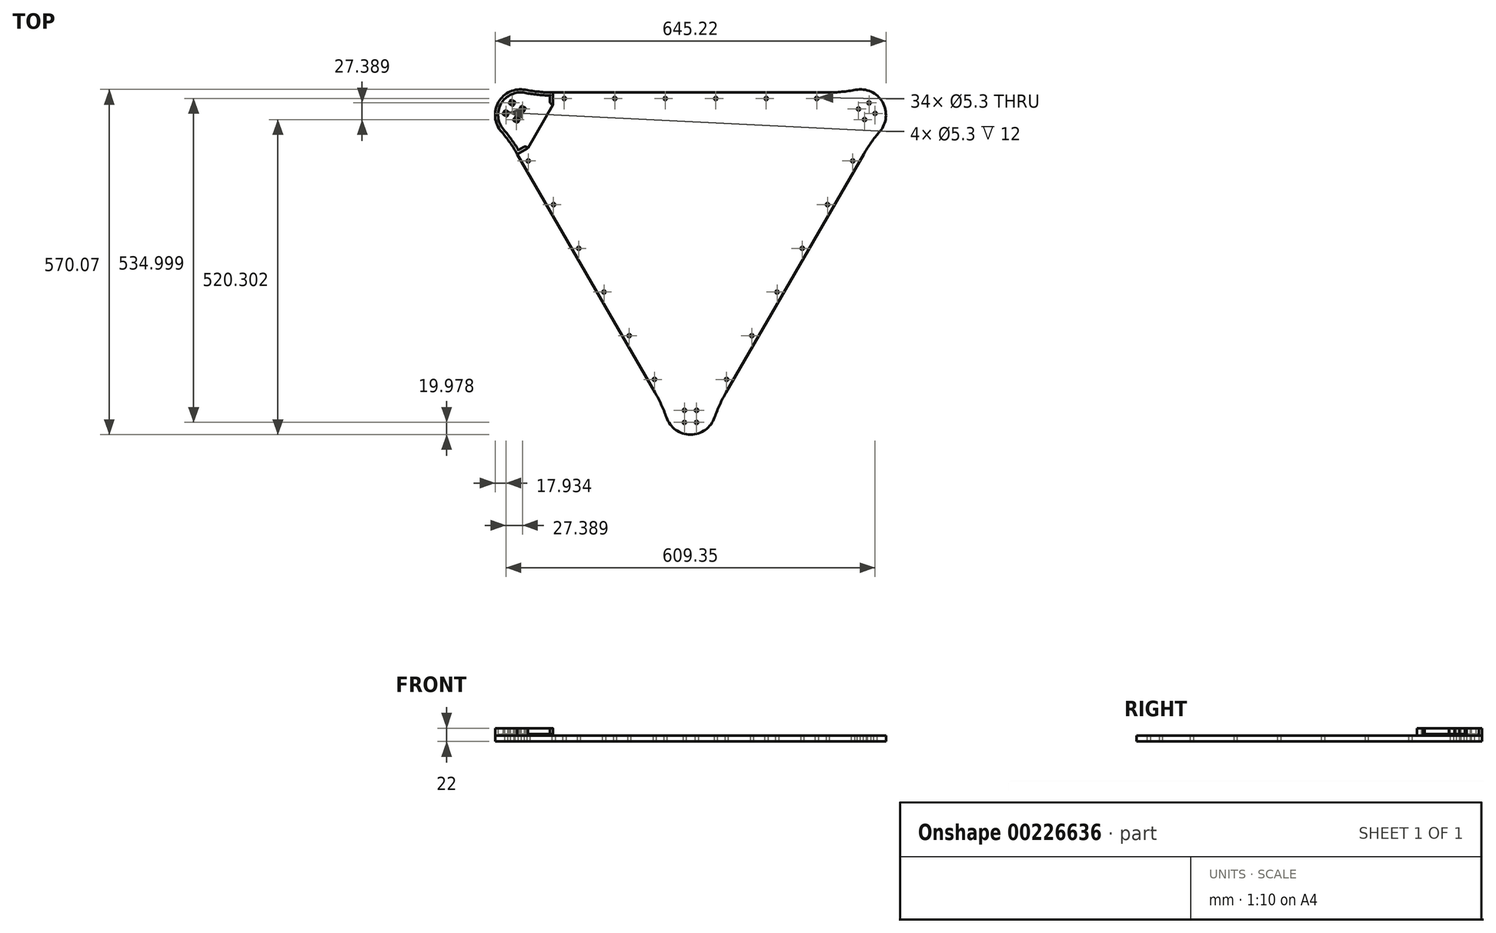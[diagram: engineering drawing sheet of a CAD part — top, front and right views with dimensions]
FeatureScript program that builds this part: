
annotation { "Feature Type Name" : "Feature", "Feature Type Description" : "" }
export const myFeature = defineFeature(function(context is Context, id is Id, definition is map)
    precondition{}
    {
        {
            var Q0;
            Q0=qCreatedBy(makeId("Top.planeOp"),FACE);
            var sketch = newSketch(context, id + "F0", { "sketchPlane" : qUnion([Q0])});
            skLineSegment(sketch, "E0", {"start": v(21.46, 15.98) * mm, "end": v(-18.54, 15.98) * mm});
            skLineSegment(sketch, "E1", {"start": v(-18.54, 15.98) * mm, "end": v(-48.54, 67.94) * mm});
            skLineSegment(sketch, "E2", {"start": v(-18.54, 15.98) * mm, "end": v(-28.54, 15.98) * mm});
            skLineSegment(sketch, "E3", {"start": v(-28.54, 15.98) * mm, "end": v(-58.54, 67.94) * mm});
            skLineSegment(sketch, "E4", {"start": v(-58.54, 67.94) * mm, "end": v(-48.54, 67.94) * mm});
            skLineSegment(sketch, "E5", {"start": v(21.46, 15.98) * mm, "end": v(51.46, 67.94) * mm});
            skLineSegment(sketch, "E6", {"start": v(21.46, 15.98) * mm, "end": v(31.46, 15.98) * mm});
            skLineSegment(sketch, "E7", {"start": v(31.46, 15.98) * mm, "end": v(61.46, 67.94) * mm});
            skLineSegment(sketch, "E8", {"start": v(61.46, 67.94) * mm, "end": v(51.46, 67.94) * mm});
            skLineSegment(sketch, "E9", {"start": v(-28.54, 15.98) * mm, "end": v(-45.86, 5.98) * mm});
            skLineSegment(sketch, "E10", {"start": v(31.46, 15.98) * mm, "end": v(48.78, 5.98) * mm});
            skLineSegment(sketch, "E11", {"start": v(-28.54, 15.98) * mm, "end": v(-28.54, -44.02) * mm});
            skLineSegment(sketch, "E12", {"start": v(-28.54, -44.02) * mm, "end": v(-18.54, -44.02) * mm});
            skLineSegment(sketch, "E13", {"start": v(-18.54, -44.02) * mm, "end": v(21.46, -44.02) * mm});
            skLineSegment(sketch, "E14", {"start": v(31.46, 15.98) * mm, "end": v(31.46, -44.02) * mm});
            skLineSegment(sketch, "E15", {"start": v(31.46, -44.02) * mm, "end": v(21.46, -44.02) * mm});
            skLineSegment(sketch, "E16", {"start": v(-45.86, 5.98) * mm, "end": v(-28.54, -44.02) * mm});
            skLineSegment(sketch, "E17", {"start": v(48.78, 5.98) * mm, "end": v(31.46, -44.02) * mm});
            skLineSegment(sketch, "E18", {"start": v(61.46, 67.94) * mm, "end": v(56.46, 67.94) * mm});
            skLineSegment(sketch, "E19", {"start": v(-58.54, 67.94) * mm, "end": v(-53.54, 67.94) * mm});
            skCircle(sketch, "E20", {"center": v(-53.54, 67.94) * mm, "radius": 12.5 * mm});
            skCircle(sketch, "E21", {"center": v(56.46, 67.94) * mm, "radius": 12.5 * mm});
            skLineSegment(sketch, "E22", {"start": v(35.32, 39.98) * mm, "end": v(-32.4, 39.98) * mm});
            skLineSegment(sketch, "E23", {"start": v(-35.86, 45.98) * mm, "end": v(38.78, 45.98) * mm});
            skLineSegment(sketch, "E24", {"start": v(-28.54, 15.98) * mm, "end": v(-18.6, 15.98) * mm});
            skLineSegment(sketch, "E25", {"start": v(21.5, -34.07) * mm, "end": v(21.5, 6.03) * mm});
            skLineSegment(sketch, "E26", {"start": v(21.5, 6.03) * mm, "end": v(15.97, 6.03) * mm});
            skLineSegment(sketch, "E27", {"start": v(15.97, 6.03) * mm, "end": v(14.18, 6.03) * mm});
            skLineSegment(sketch, "E28", {"start": v(14.18, 6.03) * mm, "end": v(8.78, 6.03) * mm});
            skLineSegment(sketch, "E29", {"start": v(8.78, 6.03) * mm, "end": v(7, 6.03) * mm});
            skLineSegment(sketch, "E30", {"start": v(7, 6.03) * mm, "end": v(-4.08, 6.03) * mm});
            skLineSegment(sketch, "E31", {"start": v(-4.08, 6.03) * mm, "end": v(-5.87, 6.03) * mm});
            skLineSegment(sketch, "E32", {"start": v(-5.87, 6.03) * mm, "end": v(-11.27, 6.03) * mm});
            skLineSegment(sketch, "E33", {"start": v(-11.27, 6.03) * mm, "end": v(-13.06, 6.03) * mm});
            skLineSegment(sketch, "E34", {"start": v(21.5, 6.03) * mm, "end": v(21.5, 4.24) * mm});
            skLineSegment(sketch, "E35", {"start": v(8.78, 4.24) * mm, "end": v(14.18, 4.24) * mm});
            skLineSegment(sketch, "E36", {"start": v(14.18, 4.24) * mm, "end": v(15.97, 6.03) * mm});
            skLineSegment(sketch, "E37", {"start": v(7, 6.03) * mm, "end": v(8.78, 4.24) * mm});
            skLineSegment(sketch, "E38", {"start": v(-5.87, 4.24) * mm, "end": v(-11.27, 4.24) * mm});
            skLineSegment(sketch, "E39", {"start": v(-11.27, 4.24) * mm, "end": v(-13.06, 6.03) * mm});
            skLineSegment(sketch, "E40", {"start": v(-5.87, 4.24) * mm, "end": v(-4.08, 6.03) * mm});
            skLineSegment(sketch, "E41", {"start": v(21.5, -34.07) * mm, "end": v(21.5, -32.28) * mm});
            skLineSegment(sketch, "E42", {"start": v(21.5, -34.07) * mm, "end": v(19.72, -34.07) * mm});
            skLineSegment(sketch, "E43", {"start": v(-18.6, -34.07) * mm, "end": v(-16.8, -34.07) * mm});
            skLineSegment(sketch, "E44", {"start": v(-11.27, -32.28) * mm, "end": v(-5.87, -32.28) * mm});
            skLineSegment(sketch, "E45", {"start": v(-5.87, -32.28) * mm, "end": v(-4.08, -34.07) * mm});
            skLineSegment(sketch, "E46", {"start": v(-11.27, -32.28) * mm, "end": v(-13.06, -34.07) * mm});
            skLineSegment(sketch, "E47", {"start": v(7, -34.07) * mm, "end": v(8.78, -32.28) * mm});
            skLineSegment(sketch, "E48", {"start": v(8.78, -32.28) * mm, "end": v(14.18, -32.28) * mm});
            skLineSegment(sketch, "E49", {"start": v(14.18, -32.28) * mm, "end": v(15.97, -34.07) * mm});
            skLineSegment(sketch, "E50", {"start": v(-18.6, 6.03) * mm, "end": v(-18.6, 0.5) * mm});
            skLineSegment(sketch, "E51", {"start": v(-18.6, 0.5) * mm, "end": v(-18.6, -1.3) * mm});
            skLineSegment(sketch, "E52", {"start": v(-18.6, -1.3) * mm, "end": v(-18.6, -6.7) * mm});
            skLineSegment(sketch, "E53", {"start": v(-18.6, -6.7) * mm, "end": v(-18.6, -8.48) * mm});
            skLineSegment(sketch, "E54", {"start": v(-18.6, -8.48) * mm, "end": v(-18.6, -19.55) * mm});
            skLineSegment(sketch, "E55", {"start": v(-18.6, -19.55) * mm, "end": v(-18.6, -21.34) * mm});
            skLineSegment(sketch, "E56", {"start": v(-18.6, -21.34) * mm, "end": v(-18.6, -26.74) * mm});
            skLineSegment(sketch, "E57", {"start": v(-18.6, -26.74) * mm, "end": v(-18.6, -28.53) * mm});
            skLineSegment(sketch, "E58", {"start": v(-18.6, 0.5) * mm, "end": v(-16.8, -1.3) * mm});
            skLineSegment(sketch, "E59", {"start": v(-16.8, -1.3) * mm, "end": v(-16.8, -6.7) * mm});
            skLineSegment(sketch, "E60", {"start": v(-16.8, -6.7) * mm, "end": v(-18.6, -8.48) * mm});
            skLineSegment(sketch, "E61", {"start": v(-18.6, -19.55) * mm, "end": v(-16.8, -21.34) * mm});
            skLineSegment(sketch, "E62", {"start": v(-16.8, -21.34) * mm, "end": v(-16.8, -26.74) * mm});
            skLineSegment(sketch, "E63", {"start": v(-16.8, -26.74) * mm, "end": v(-18.6, -28.53) * mm});
            skLineSegment(sketch, "E64", {"start": v(21.5, 0.5) * mm, "end": v(19.72, -1.3) * mm});
            skLineSegment(sketch, "E65", {"start": v(19.72, -1.3) * mm, "end": v(19.72, -6.7) * mm});
            skLineSegment(sketch, "E66", {"start": v(19.72, -6.7) * mm, "end": v(21.5, -8.48) * mm});
            skLineSegment(sketch, "E67", {"start": v(21.5, -19.55) * mm, "end": v(19.72, -21.34) * mm});
            skLineSegment(sketch, "E68", {"start": v(19.72, -21.34) * mm, "end": v(19.72, -26.74) * mm});
            skLineSegment(sketch, "E69", {"start": v(19.72, -26.74) * mm, "end": v(21.5, -28.53) * mm});
            skLineSegment(sketch, "E70", {"start": v(-18.6, 6.03) * mm, "end": v(21.5, 6.03) * mm});
            skLineSegment(sketch, "E71", {"start": v(21.5, 6.03) * mm, "end": v(21.5, -34.07) * mm});
            skLineSegment(sketch, "E72", {"start": v(21.5, -34.07) * mm, "end": v(-18.6, -34.07) * mm});
            skLineSegment(sketch, "E73", {"start": v(-18.6, 6.03) * mm, "end": v(-18.6, -34.07) * mm});
            skSolve(sketch);
        }
        {
            var Q0;
            Q0=qCreatedBy(makeId("Top.planeOp"),FACE);
            var sketch = newSketch(context, id + "F1", { "sketchPlane" : qUnion([Q0])});
            skLineSegment(sketch, "E74", {"start": v(-45.86, 5.98) * mm, "end": v(-170.86, 222.49) * mm});
            skLineSegment(sketch, "E75", {"start": v(-170.86, 222.49) * mm, "end": v(-153.54, 232.49) * mm});
            skLineSegment(sketch, "E76", {"start": v(-153.54, 232.49) * mm, "end": v(-28.54, 15.98) * mm});
            skLineSegment(sketch, "E77", {"start": v(-28.54, 15.98) * mm, "end": v(-45.86, 5.98) * mm});
            skLineSegment(sketch, "E78", {"start": v(48.78, 5.98) * mm, "end": v(173.78, 222.49) * mm});
            skLineSegment(sketch, "E79", {"start": v(173.78, 222.49) * mm, "end": v(156.46, 232.49) * mm});
            skLineSegment(sketch, "E80", {"start": v(156.46, 232.49) * mm, "end": v(31.46, 15.98) * mm});
            skLineSegment(sketch, "E81", {"start": v(31.46, 15.98) * mm, "end": v(48.78, 5.98) * mm});
            skLineSegment(sketch, "E82", {"start": v(-153.54, 232.49) * mm, "end": v(1.46, 321.98) * mm});
            skLineSegment(sketch, "E83", {"start": v(1.46, 321.98) * mm, "end": v(156.46, 232.49) * mm});
            skLineSegment(sketch, "E84", {"start": v(-45.86, 5.98) * mm, "end": v(-28.54, -44.02) * mm});
            skLineSegment(sketch, "E85", {"start": v(-28.54, -44.02) * mm, "end": v(31.46, -44.02) * mm});
            skLineSegment(sketch, "E86", {"start": v(31.46, -44.02) * mm, "end": v(48.78, 5.98) * mm});
            skCircle(sketch, "E87", {"center": v(60.95, 47.07) * mm, "radius": 2.65 * mm});
            skCircle(sketch, "E88", {"center": v(102.62, 119.24) * mm, "radius": 2.65 * mm});
            skLineSegment(sketch, "E89", {"start": v(60.95, 47.07) * mm, "end": v(102.62, 119.24) * mm});
            skPoint(sketch, "E90", {"position": v(81.79, 83.15) * mm});
            skCircle(sketch, "E91", {"center": v(144.29, 191.4) * mm, "radius": 2.65 * mm});
            skLineSegment(sketch, "E92", {"start": v(144.29, 191.4) * mm, "end": v(102.62, 119.24) * mm});
            skCircle(sketch, "E93", {"center": v(-141.37, 191.4) * mm, "radius": 2.65 * mm});
            skCircle(sketch, "E94", {"center": v(-99.7, 119.24) * mm, "radius": 2.65 * mm});
            skCircle(sketch, "E95", {"center": v(-58.03, 47.07) * mm, "radius": 2.65 * mm});
            skLineSegment(sketch, "E96", {"start": v(-141.37, 191.4) * mm, "end": v(-99.7, 119.24) * mm});
            skLineSegment(sketch, "E97", {"start": v(-99.7, 119.24) * mm, "end": v(-58.03, 47.07) * mm});
            skCircle(sketch, "E98", {"center": v(-8.57, -4) * mm, "radius": 2.65 * mm});
            skCircle(sketch, "E99", {"center": v(11.48, -4) * mm, "radius": 2.65 * mm});
            skCircle(sketch, "E100", {"center": v(-8.57, -24.04) * mm, "radius": 2.65 * mm});
            skCircle(sketch, "E101", {"center": v(11.48, -24.04) * mm, "radius": 2.65 * mm});
            skPoint(sketch, "E102", {"position": v(-8.57, 4.24) * mm});
            skPoint(sketch, "E103", {"position": v(11.48, 4.24) * mm});
            skPoint(sketch, "E104", {"position": v(-16.8, -4) * mm});
            skPoint(sketch, "E105", {"position": v(-16.8, -24.04) * mm});
            skArc(sketch, "E106", {"start": v(-38.36, -15.67) * mm, "mid": v(1.46, -44.02) * mm, "end": v(41.28, -15.67) * mm});
            skSolve(sketch);
        }
        {
            var Q0;
            Q0=makeQuery(id+"F1.imprint","IMPRINT",FACE,{"disambiguationData":[TD([[makeQuery(id+"F1.imprint","IMPRINT",EDGE,{"derivedFrom":sQuery(id+"F1.wireOp",EDGE,"E76")}),1.0]])]});
            var Q1;
            Q1=makeQuery(id+"F1.imprint","IMPRINT",FACE,{"disambiguationData":[TD([[makeQuery(id+"F1.imprint","IMPRINT",EDGE,{"derivedFrom":sQuery(id+"F1.wireOp",EDGE,"E74")}),-1.0]])]});
            var Q2;
            Q2=makeQuery(id+"F1.imprint","IMPRINT",FACE,{"disambiguationData":[TD([[makeQuery(id+"F1.imprint","IMPRINT",EDGE,{"derivedFrom":sQuery(id+"F1.wireOp",EDGE,"E78")}),1.0]])]});
            extrude(context, id + "F2", {"entities" : qUnion([Q0, Q1, Q2]), "depth" : 10 * mm});
        }
        {
            var Q0;
            Q0=makeQuery(id+"F2.opExtrude","SWEPT_EDGE",EDGE,{"disambiguationData":[OSD([sQuery(id+"F1.wireOp",EDGE,"E78"),sQuery(id+"F1.wireOp",EDGE,"E81"),sQuery(id+"F1.wireOp",EDGE,"E86")])]});
            var Q1;
            Q1=makeQuery(id+"F2.opExtrude","SWEPT_EDGE",EDGE,{"disambiguationData":[OSD([sQuery(id+"F1.wireOp",EDGE,"E74"),sQuery(id+"F1.wireOp",EDGE,"E77"),sQuery(id+"F1.wireOp",EDGE,"E84")])]});
            fillet(context, id + "F3", {"entities" : qUnion([Q0, Q1]), "radius" : 240 * mm, "tangentPropagation" : true, "allowEdgeOverflow" : false});
        }
        {
            var Q0;
            Q0=makeQuery(id+"F2.opExtrude","SWEPT_BODY",BODY,{"disambiguationData":[OSD([sQuery(id+"F1.wireOp",EDGE,"E74"),sQuery(id+"F1.wireOp",EDGE,"E75"),sQuery(id+"F1.wireOp",EDGE,"E78"),sQuery(id+"F1.wireOp",EDGE,"E79"),sQuery(id+"F1.wireOp",EDGE,"E82"),sQuery(id+"F1.wireOp",EDGE,"E83"),sQuery(id+"F1.wireOp",EDGE,"E84"),sQuery(id+"F1.wireOp",EDGE,"E85"),sQuery(id+"F1.wireOp",EDGE,"E86"),sQuery(id+"F1.wireOp",EDGE,"E87"),sQuery(id+"F1.wireOp",EDGE,"E88"),sQuery(id+"F1.wireOp",EDGE,"E91"),sQuery(id+"F1.wireOp",EDGE,"E93"),sQuery(id+"F1.wireOp",EDGE,"E94"),sQuery(id+"F1.wireOp",EDGE,"E95"),sQuery(id+"F1.wireOp",EDGE,"E98"),sQuery(id+"F1.wireOp",EDGE,"E99"),sQuery(id+"F1.wireOp",EDGE,"E100"),sQuery(id+"F1.wireOp",EDGE,"E101")])]});
            var Q1;
            Q1=makeQuery(id+"F2.opExtrude","SWEPT_EDGE",EDGE,{"disambiguationData":[OSD([sQuery(id+"F1.wireOp",EDGE,"E82"),sQuery(id+"F1.wireOp",EDGE,"E83")])]});
            circularPattern(context, id + "F4", {"operationType" : NewBodyOperationType.ADD, "entities" : qUnion([Q0]), "axis" : qUnion([Q1]), "angle" : 360 * degree, "instanceCount" : 3, "equalSpace" : true});
        }
        {
            var Q0;
            {var subQ0=makeQuery(id+"F2.opExtrude","CAP_FACE",FACE,{"disambiguationData":[OSD([sQuery(id+"F1.wireOp",EDGE,"E74"),sQuery(id+"F1.wireOp",EDGE,"E75"),sQuery(id+"F1.wireOp",EDGE,"E78"),sQuery(id+"F1.wireOp",EDGE,"E79"),sQuery(id+"F1.wireOp",EDGE,"E82"),sQuery(id+"F1.wireOp",EDGE,"E83"),sQuery(id+"F1.wireOp",EDGE,"E84"),sQuery(id+"F1.wireOp",EDGE,"E86"),sQuery(id+"F1.wireOp",EDGE,"E87"),sQuery(id+"F1.wireOp",EDGE,"E88"),sQuery(id+"F1.wireOp",EDGE,"E91"),sQuery(id+"F1.wireOp",EDGE,"E93"),sQuery(id+"F1.wireOp",EDGE,"E94"),sQuery(id+"F1.wireOp",EDGE,"E95"),sQuery(id+"F1.wireOp",EDGE,"E98"),sQuery(id+"F1.wireOp",EDGE,"E99"),sQuery(id+"F1.wireOp",EDGE,"E100"),sQuery(id+"F1.wireOp",EDGE,"E101"),sQuery(id+"F1.wireOp",EDGE,"E106")])],"isStart":false});Q0=makeQuery(id+"F4.boolean.opBoolean","MERGE",FACE,{"derivedFrom":[subQ0,makeQuery(id+"F4.opPattern","COPY",FACE,{"derivedFrom":subQ0,"instanceName":"1"}),makeQuery(id+"F4.opPattern","COPY",FACE,{"derivedFrom":subQ0,"instanceName":"2"})]});}
            var sketch = newSketch(context, id + "F5", { "sketchPlane" : qUnion([Q0])});
            skArc(sketch, "E107", {"start": v(-271.01, 525.28) * mm, "mid": v(-315.5, 504.98) * mm, "end": v(-310.84, 456.3) * mm});
            skArc(sketch, "E108", {"start": v(313.78, 456.32) * mm, "mid": v(318.42, 504.98) * mm, "end": v(273.96, 525.29) * mm});
            skArc(sketch, "E109", {"start": v(-38.36, -15.67) * mm, "mid": v(1.47, -44.02) * mm, "end": v(41.29, -15.64) * mm});
            skArc(sketch, "E110", {"start": v(-38.36, -15.67) * mm, "mid": v(-46.84, 5.52) * mm, "end": v(-57.3, 25.8) * mm});
            skArc(sketch, "E111", {"start": v(60.22, 25.8) * mm, "mid": v(49.77, 5.53) * mm, "end": v(41.29, -15.64) * mm});
            skArc(sketch, "E112", {"start": v(-284.42, 419.18) * mm, "mid": v(-296.75, 438.36) * mm, "end": v(-310.84, 456.3) * mm});
            skArc(sketch, "E113", {"start": v(-271.01, 525.28) * mm, "mid": v(-248.44, 522.04) * mm, "end": v(-225.66, 520.96) * mm});
            skArc(sketch, "E114", {"start": v(228.58, 520.96) * mm, "mid": v(251.37, 522.04) * mm, "end": v(273.96, 525.29) * mm});
            skArc(sketch, "E115", {"start": v(313.78, 456.32) * mm, "mid": v(299.68, 438.38) * mm, "end": v(287.34, 419.18) * mm});
            skLineSegment(sketch, "E116", {"start": v(60.22, 25.8) * mm, "end": v(287.34, 419.18) * mm});
            skLineSegment(sketch, "E117", {"start": v(228.58, 520.96) * mm, "end": v(-225.66, 520.96) * mm});
            skLineSegment(sketch, "E118", {"start": v(-284.42, 419.18) * mm, "end": v(-57.3, 25.8) * mm});
            skCircle(sketch, "E119", {"center": v(-8.57, -24.04) * mm, "radius": 2.65 * mm});
            skCircle(sketch, "E120", {"center": v(11.48, -24.04) * mm, "radius": 2.65 * mm});
            skCircle(sketch, "E121", {"center": v(-8.57, -4) * mm, "radius": 2.65 * mm});
            skCircle(sketch, "E122", {"center": v(60.95, 47.07) * mm, "radius": 2.65 * mm});
            skCircle(sketch, "E123", {"center": v(102.62, 119.24) * mm, "radius": 2.65 * mm});
            skCircle(sketch, "E124", {"center": v(144.29, 191.4) * mm, "radius": 2.65 * mm});
            skCircle(sketch, "E125", {"center": v(185.95, 263.57) * mm, "radius": 2.65 * mm});
            skCircle(sketch, "E126", {"center": v(227.62, 335.74) * mm, "radius": 2.65 * mm});
            skCircle(sketch, "E127", {"center": v(269.29, 407.91) * mm, "radius": 2.65 * mm});
            skCircle(sketch, "E128", {"center": v(288.77, 476.28) * mm, "radius": 2.65 * mm});
            skCircle(sketch, "E129", {"center": v(306.13, 486.3) * mm, "radius": 2.65 * mm});
            skCircle(sketch, "E130", {"center": v(296.1, 503.67) * mm, "radius": 2.65 * mm});
            skCircle(sketch, "E131", {"center": v(278.75, 493.65) * mm, "radius": 2.65 * mm});
            skCircle(sketch, "E132", {"center": v(209.8, 510.96) * mm, "radius": 2.65 * mm});
            skCircle(sketch, "E133", {"center": v(126.46, 510.96) * mm, "radius": 2.65 * mm});
            skCircle(sketch, "E134", {"center": v(43.13, 510.96) * mm, "radius": 2.65 * mm});
            skCircle(sketch, "E135", {"center": v(-40.2, 510.96) * mm, "radius": 2.65 * mm});
            skCircle(sketch, "E136", {"center": v(-123.54, 510.96) * mm, "radius": 2.65 * mm});
            skCircle(sketch, "E137", {"center": v(-206.87, 510.96) * mm, "radius": 2.65 * mm});
            skCircle(sketch, "E138", {"center": v(-293.2, 503.67) * mm, "radius": 2.65 * mm});
            skCircle(sketch, "E139", {"center": v(-275.83, 493.65) * mm, "radius": 2.65 * mm});
            skCircle(sketch, "E140", {"center": v(-303.22, 486.3) * mm, "radius": 2.65 * mm});
            skCircle(sketch, "E141", {"center": v(-285.85, 476.28) * mm, "radius": 2.65 * mm});
            skCircle(sketch, "E142", {"center": v(-266.37, 407.91) * mm, "radius": 2.65 * mm});
            skCircle(sketch, "E143", {"center": v(-224.7, 335.74) * mm, "radius": 2.65 * mm});
            skCircle(sketch, "E144", {"center": v(-183.03, 263.57) * mm, "radius": 2.65 * mm});
            skCircle(sketch, "E145", {"center": v(-141.37, 191.4) * mm, "radius": 2.65 * mm});
            skCircle(sketch, "E146", {"center": v(-99.7, 119.24) * mm, "radius": 2.65 * mm});
            skCircle(sketch, "E147", {"center": v(-58.03, 47.07) * mm, "radius": 2.65 * mm});
            skCircle(sketch, "E148", {"center": v(11.48, -4) * mm, "radius": 2.65 * mm});
            skLineSegment(sketch, "E149", {"start": v(-284.42, 419.18) * mm, "end": v(-267.1, 429.18) * mm});
            skPoint(sketch, "E150", {"position": v(-275.76, 424.18) * mm});
            skLineSegment(sketch, "E151", {"start": v(-57.3, 25.8) * mm, "end": v(-39.98, 35.8) * mm});
            skLineSegment(sketch, "E152", {"start": v(-39.98, 35.8) * mm, "end": v(-267.1, 429.18) * mm});
            skPoint(sketch, "E153", {"position": v(-48.64, 30.8) * mm});
            skLineSegment(sketch, "E154", {"start": v(-48.64, 30.8) * mm, "end": v(-275.76, 424.18) * mm});
            skLineSegment(sketch, "E155", {"start": v(60.22, 25.8) * mm, "end": v(42.9, 35.8) * mm});
            skLineSegment(sketch, "E156", {"start": v(42.9, 35.8) * mm, "end": v(270.02, 429.18) * mm});
            skLineSegment(sketch, "E157", {"start": v(270.02, 429.18) * mm, "end": v(287.34, 419.18) * mm});
            skLineSegment(sketch, "E158", {"start": v(278.68, 424.18) * mm, "end": v(51.56, 30.8) * mm});
            skLineSegment(sketch, "E159", {"start": v(-225.66, 520.96) * mm, "end": v(-225.66, 500.96) * mm});
            skLineSegment(sketch, "E160", {"start": v(-225.66, 500.96) * mm, "end": v(228.58, 500.96) * mm});
            skLineSegment(sketch, "E161", {"start": v(228.58, 500.96) * mm, "end": v(228.58, 520.96) * mm});
            skLineSegment(sketch, "E162", {"start": v(-225.66, 510.96) * mm, "end": v(228.58, 510.96) * mm});
            skSolve(sketch);
        }
        {
            var Q0;
            {var subQ12=sQuery(id+"F5.wireOp",EDGE,"E108");Q0=makeQuery(id+"F5.imprint","IMPRINT",FACE,{"disambiguationData":[TD([[makeQuery(id+"F5.imprint","IMPRINT",EDGE,{"derivedFrom":subQ12}),1.0]])]});}
            var sketch = newSketch(context, id + "F6", { "sketchPlane" : qUnion([Q0])});
            skLineSegment(sketch, "E163.bottom", {"start": v(-321.15, 526.05) * mm, "end": v(324.07, 526.05) * mm});
            skLineSegment(sketch, "E163.top", {"start": v(-321.15, -44.02) * mm, "end": v(324.07, -44.02) * mm});
            skLineSegment(sketch, "E163.left", {"start": v(-321.15, 526.05) * mm, "end": v(-321.15, -44.02) * mm});
            skLineSegment(sketch, "E163.right", {"start": v(324.07, 526.05) * mm, "end": v(324.07, -44.02) * mm});
            skSolve(sketch);
        }
        {
            var Q0;
            {var subQ24=sQuery(id+"F5.wireOp",EDGE,"E111");Q0=makeQuery(id+"F6.imprint","IMPRINT",FACE,{"disambiguationData":[TD([[makeQuery(id+"F6.imprint","IMPRINT",EDGE,{"derivedFrom":makeQuery(id+"F5.imprint","IMPRINT",EDGE,{"derivedFrom":subQ24})}),1.0]])]});}
            var sketch = newSketch(context, id + "F7", { "sketchPlane" : qUnion([Q0])});
            skCircle(sketch, "E164", {"center": v(854.61, 468.1) * mm, "radius": 2.65 * mm});
            skCircle(sketch, "E165", {"center": v(771.28, 468.1) * mm, "radius": 2.65 * mm});
            skCircle(sketch, "E166", {"center": v(687.94, 468.1) * mm, "radius": 2.65 * mm});
            skCircle(sketch, "E167", {"center": v(604.61, 468.1) * mm, "radius": 2.65 * mm});
            skCircle(sketch, "E168", {"center": v(521.28, 468.1) * mm, "radius": 2.65 * mm});
            skCircle(sketch, "E169", {"center": v(437.94, 468.1) * mm, "radius": 2.65 * mm});
            skLineSegment(sketch, "E170", {"start": v(419.16, 478.1) * mm, "end": v(419.16, 458.1) * mm});
            skLineSegment(sketch, "E171", {"start": v(419.16, 458.1) * mm, "end": v(873.4, 458.1) * mm});
            skLineSegment(sketch, "E172", {"start": v(873.4, 458.1) * mm, "end": v(873.4, 478.1) * mm});
            skLineSegment(sketch, "E173", {"start": v(419.16, 478.1) * mm, "end": v(873.4, 478.1) * mm});
            skPoint(sketch, "E174.orphan", {"position": v(419.16, 468.1) * mm});
            skPoint(sketch, "E175.trimOffspring.end.orphan", {"position": v(873.4, 468.1) * mm});
            skArc(sketch, "E176", {"start": v(-225.66, 520.96) * mm, "mid": v(-248.44, 522.04) * mm, "end": v(-271.01, 525.28) * mm});
            skArc(sketch, "E177", {"start": v(-284.42, 419.18) * mm, "mid": v(-296.75, 438.36) * mm, "end": v(-310.84, 456.3) * mm});
            skArc(sketch, "E178", {"start": v(-271.01, 525.28) * mm, "mid": v(-315.5, 504.98) * mm, "end": v(-310.84, 456.3) * mm});
            skLineSegment(sketch, "E179", {"start": v(-284.42, 419.18) * mm, "end": v(-267.1, 429.18) * mm});
            skLineSegment(sketch, "E180", {"start": v(-267.1, 429.18) * mm, "end": v(-225.66, 500.96) * mm});
            skLineSegment(sketch, "E181", {"start": v(-225.66, 500.96) * mm, "end": v(-225.66, 520.96) * mm});
            skCircle(sketch, "E182", {"center": v(-275.83, 493.65) * mm, "radius": 3.9 * mm});
            skCircle(sketch, "E183", {"center": v(-293.2, 503.67) * mm, "radius": 3.9 * mm});
            skCircle(sketch, "E184", {"center": v(-303.22, 486.3) * mm, "radius": 3.9 * mm});
            skCircle(sketch, "E185", {"center": v(-285.85, 476.28) * mm, "radius": 3.9 * mm});
            skLineSegment(sketch, "E186", {"start": v(-281.15, 492.22) * mm, "end": v(-274.4, 488.32) * mm});
            skLineSegment(sketch, "E187", {"start": v(-274.4, 488.32) * mm, "end": v(-270.5, 495.07) * mm});
            skLineSegment(sketch, "E188", {"start": v(-270.5, 495.07) * mm, "end": v(-277.25, 498.97) * mm});
            skLineSegment(sketch, "E189", {"start": v(-277.25, 498.97) * mm, "end": v(-281.15, 492.22) * mm});
            skLineSegment(sketch, "E190", {"start": v(-298.52, 502.24) * mm, "end": v(-291.76, 498.34) * mm});
            skLineSegment(sketch, "E191", {"start": v(-291.76, 498.34) * mm, "end": v(-287.86, 505.1) * mm});
            skLineSegment(sketch, "E192", {"start": v(-287.86, 505.1) * mm, "end": v(-294.62, 509) * mm});
            skLineSegment(sketch, "E193", {"start": v(-294.62, 509) * mm, "end": v(-298.52, 502.24) * mm});
            skLineSegment(sketch, "E194", {"start": v(-304.64, 491.63) * mm, "end": v(-308.54, 484.88) * mm});
            skLineSegment(sketch, "E195", {"start": v(-308.54, 484.88) * mm, "end": v(-301.79, 480.98) * mm});
            skLineSegment(sketch, "E196", {"start": v(-301.79, 480.98) * mm, "end": v(-297.89, 487.73) * mm});
            skLineSegment(sketch, "E197", {"start": v(-297.89, 487.73) * mm, "end": v(-304.64, 491.63) * mm});
            skLineSegment(sketch, "E198", {"start": v(-291.18, 474.85) * mm, "end": v(-287.28, 481.6) * mm});
            skLineSegment(sketch, "E199", {"start": v(-287.28, 481.6) * mm, "end": v(-280.52, 477.7) * mm});
            skLineSegment(sketch, "E200", {"start": v(-280.52, 477.7) * mm, "end": v(-284.42, 470.95) * mm});
            skLineSegment(sketch, "E201", {"start": v(-284.42, 470.95) * mm, "end": v(-291.18, 474.85) * mm});
            skSolve(sketch);
        }
        {
            var Q0;
            Q0=makeQuery(id+"F7.imprint","IMPRINT",FACE,{"disambiguationData":[TD([[makeQuery(id+"F7.imprint","IMPRINT",EDGE,{"derivedFrom":makeQuery(id+"F6.imprint","IMPRINT",EDGE,{"derivedFrom":makeQuery(id+"F5.imprint","IMPRINT",EDGE,{"derivedFrom":sQuery(id+"F5.wireOp",EDGE,"E140")})})}),-1.0]])]});
            var Q1;
            {var subQ0=sQuery(id+"F7.wireOp",EDGE,"E194");var subQ1=sQuery(id+"F7.wireOp",EDGE,"E184");var subQ2=makeQuery(id+"F7.imprint","INTERSECT",VERTEX,{"derivedFrom":[subQ1,subQ0]});Q1=makeQuery(id+"F7.imprint","IMPRINT",FACE,{"disambiguationData":[TD([[makeQuery(id+"F7.imprint","IMPRINT",EDGE,{"disambiguationData":[TD([[subQ2,1.0]])],"derivedFrom":subQ1}),-1.0]])]});}
            var Q2;
            {var subQ0=sQuery(id+"F7.wireOp",EDGE,"E197");var subQ1=sQuery(id+"F7.wireOp",EDGE,"E184");var subQ2=makeQuery(id+"F7.imprint","INTERSECT",VERTEX,{"derivedFrom":[subQ1,subQ0]});Q2=makeQuery(id+"F7.imprint","IMPRINT",FACE,{"disambiguationData":[TD([[makeQuery(id+"F7.imprint","IMPRINT",EDGE,{"disambiguationData":[TD([[subQ2,1.0]])],"derivedFrom":subQ1}),-1.0]])]});}
            var Q3;
            {var subQ0=sQuery(id+"F7.wireOp",EDGE,"E195");var subQ1=sQuery(id+"F7.wireOp",EDGE,"E184");var subQ2=makeQuery(id+"F7.imprint","INTERSECT",VERTEX,{"derivedFrom":[subQ1,subQ0]});Q3=makeQuery(id+"F7.imprint","IMPRINT",FACE,{"disambiguationData":[TD([[makeQuery(id+"F7.imprint","IMPRINT",EDGE,{"disambiguationData":[TD([[subQ2,-1.0]])],"derivedFrom":subQ1}),-1.0]])]});}
            var Q4;
            {var subQ0=sQuery(id+"F7.wireOp",EDGE,"E194");var subQ1=sQuery(id+"F7.wireOp",EDGE,"E184");var subQ2=makeQuery(id+"F7.imprint","INTERSECT",VERTEX,{"derivedFrom":[subQ1,subQ0]});Q4=makeQuery(id+"F7.imprint","IMPRINT",FACE,{"disambiguationData":[TD([[makeQuery(id+"F7.imprint","IMPRINT",EDGE,{"disambiguationData":[TD([[subQ2,-1.0]])],"derivedFrom":subQ1}),-1.0]])]});}
            var Q5;
            Q5=makeQuery(id+"F7.imprint","IMPRINT",FACE,{"disambiguationData":[TD([[makeQuery(id+"F7.imprint","IMPRINT",EDGE,{"derivedFrom":makeQuery(id+"F6.imprint","IMPRINT",EDGE,{"derivedFrom":makeQuery(id+"F5.imprint","IMPRINT",EDGE,{"derivedFrom":sQuery(id+"F5.wireOp",EDGE,"E141")})})}),-1.0]])]});
            var Q6;
            {var subQ0=sQuery(id+"F7.wireOp",EDGE,"E198");var subQ1=sQuery(id+"F7.wireOp",EDGE,"E185");var subQ2=makeQuery(id+"F7.imprint","INTERSECT",VERTEX,{"derivedFrom":[subQ1,subQ0]});Q6=makeQuery(id+"F7.imprint","IMPRINT",FACE,{"disambiguationData":[TD([[makeQuery(id+"F7.imprint","IMPRINT",EDGE,{"disambiguationData":[TD([[subQ2,1.0]])],"derivedFrom":subQ1}),-1.0]])]});}
            var Q7;
            {var subQ0=sQuery(id+"F7.wireOp",EDGE,"E198");var subQ1=sQuery(id+"F7.wireOp",EDGE,"E185");var subQ2=makeQuery(id+"F7.imprint","INTERSECT",VERTEX,{"derivedFrom":[subQ1,subQ0]});Q7=makeQuery(id+"F7.imprint","IMPRINT",FACE,{"disambiguationData":[TD([[makeQuery(id+"F7.imprint","IMPRINT",EDGE,{"disambiguationData":[TD([[subQ2,-1.0]])],"derivedFrom":subQ1}),-1.0]])]});}
            var Q8;
            {var subQ0=sQuery(id+"F7.wireOp",EDGE,"E201");var subQ1=sQuery(id+"F7.wireOp",EDGE,"E185");var subQ2=makeQuery(id+"F7.imprint","INTERSECT",VERTEX,{"derivedFrom":[subQ1,subQ0]});Q8=makeQuery(id+"F7.imprint","IMPRINT",FACE,{"disambiguationData":[TD([[makeQuery(id+"F7.imprint","IMPRINT",EDGE,{"disambiguationData":[TD([[subQ2,-1.0]])],"derivedFrom":subQ1}),-1.0]])]});}
            var Q9;
            {var subQ0=sQuery(id+"F7.wireOp",EDGE,"E199");var subQ1=sQuery(id+"F7.wireOp",EDGE,"E185");var subQ2=makeQuery(id+"F7.imprint","INTERSECT",VERTEX,{"derivedFrom":[subQ1,subQ0]});Q9=makeQuery(id+"F7.imprint","IMPRINT",FACE,{"disambiguationData":[TD([[makeQuery(id+"F7.imprint","IMPRINT",EDGE,{"disambiguationData":[TD([[subQ2,1.0]])],"derivedFrom":subQ1}),-1.0]])]});}
            var Q10;
            Q10=makeQuery(id+"F7.imprint","IMPRINT",FACE,{"disambiguationData":[TD([[makeQuery(id+"F7.imprint","IMPRINT",EDGE,{"derivedFrom":makeQuery(id+"F6.imprint","IMPRINT",EDGE,{"derivedFrom":makeQuery(id+"F5.imprint","IMPRINT",EDGE,{"derivedFrom":sQuery(id+"F5.wireOp",EDGE,"E139")})})}),-1.0]])]});
            var Q11;
            {var subQ0=sQuery(id+"F7.wireOp",EDGE,"E189");var subQ1=sQuery(id+"F7.wireOp",EDGE,"E182");var subQ2=makeQuery(id+"F7.imprint","INTERSECT",VERTEX,{"derivedFrom":[subQ1,subQ0]});Q11=makeQuery(id+"F7.imprint","IMPRINT",FACE,{"disambiguationData":[TD([[makeQuery(id+"F7.imprint","IMPRINT",EDGE,{"disambiguationData":[TD([[subQ2,-1.0]])],"derivedFrom":subQ1}),-1.0]])]});}
            var Q12;
            {var subQ0=sQuery(id+"F7.wireOp",EDGE,"E186");var subQ1=sQuery(id+"F7.wireOp",EDGE,"E182");var subQ2=makeQuery(id+"F7.imprint","INTERSECT",VERTEX,{"derivedFrom":[subQ1,subQ0]});Q12=makeQuery(id+"F7.imprint","IMPRINT",FACE,{"disambiguationData":[TD([[makeQuery(id+"F7.imprint","IMPRINT",EDGE,{"disambiguationData":[TD([[subQ2,-1.0]])],"derivedFrom":subQ1}),-1.0]])]});}
            var Q13;
            {var subQ0=sQuery(id+"F7.wireOp",EDGE,"E188");var subQ1=sQuery(id+"F7.wireOp",EDGE,"E182");var subQ2=makeQuery(id+"F7.imprint","INTERSECT",VERTEX,{"derivedFrom":[subQ1,subQ0]});Q13=makeQuery(id+"F7.imprint","IMPRINT",FACE,{"disambiguationData":[TD([[makeQuery(id+"F7.imprint","IMPRINT",EDGE,{"disambiguationData":[TD([[subQ2,1.0]])],"derivedFrom":subQ1}),-1.0]])]});}
            var Q14;
            {var subQ0=sQuery(id+"F7.wireOp",EDGE,"E189");var subQ1=sQuery(id+"F7.wireOp",EDGE,"E182");var subQ2=makeQuery(id+"F7.imprint","INTERSECT",VERTEX,{"derivedFrom":[subQ1,subQ0]});Q14=makeQuery(id+"F7.imprint","IMPRINT",FACE,{"disambiguationData":[TD([[makeQuery(id+"F7.imprint","IMPRINT",EDGE,{"disambiguationData":[TD([[subQ2,1.0]])],"derivedFrom":subQ1}),-1.0]])]});}
            var Q15;
            {var subQ0=sQuery(id+"F7.wireOp",EDGE,"E192");var subQ1=sQuery(id+"F7.wireOp",EDGE,"E183");var subQ2=makeQuery(id+"F7.imprint","INTERSECT",VERTEX,{"derivedFrom":[subQ1,subQ0]});Q15=makeQuery(id+"F7.imprint","IMPRINT",FACE,{"disambiguationData":[TD([[makeQuery(id+"F7.imprint","IMPRINT",EDGE,{"disambiguationData":[TD([[subQ2,1.0]])],"derivedFrom":subQ1}),-1.0]])]});}
            var Q16;
            Q16=makeQuery(id+"F7.imprint","IMPRINT",FACE,{"disambiguationData":[TD([[makeQuery(id+"F7.imprint","IMPRINT",EDGE,{"derivedFrom":makeQuery(id+"F6.imprint","IMPRINT",EDGE,{"derivedFrom":makeQuery(id+"F5.imprint","IMPRINT",EDGE,{"derivedFrom":sQuery(id+"F5.wireOp",EDGE,"E138")})})}),-1.0]])]});
            var Q17;
            {var subQ0=sQuery(id+"F7.wireOp",EDGE,"E193");var subQ1=sQuery(id+"F7.wireOp",EDGE,"E183");var subQ2=makeQuery(id+"F7.imprint","INTERSECT",VERTEX,{"derivedFrom":[subQ1,subQ0]});Q17=makeQuery(id+"F7.imprint","IMPRINT",FACE,{"disambiguationData":[TD([[makeQuery(id+"F7.imprint","IMPRINT",EDGE,{"disambiguationData":[TD([[subQ2,1.0]])],"derivedFrom":subQ1}),-1.0]])]});}
            var Q18;
            {var subQ0=sQuery(id+"F7.wireOp",EDGE,"E193");var subQ1=sQuery(id+"F7.wireOp",EDGE,"E183");var subQ2=makeQuery(id+"F7.imprint","INTERSECT",VERTEX,{"derivedFrom":[subQ1,subQ0]});Q18=makeQuery(id+"F7.imprint","IMPRINT",FACE,{"disambiguationData":[TD([[makeQuery(id+"F7.imprint","IMPRINT",EDGE,{"disambiguationData":[TD([[subQ2,-1.0]])],"derivedFrom":subQ1}),-1.0]])]});}
            var Q19;
            {var subQ0=sQuery(id+"F7.wireOp",EDGE,"E190");var subQ1=sQuery(id+"F7.wireOp",EDGE,"E183");var subQ2=makeQuery(id+"F7.imprint","INTERSECT",VERTEX,{"derivedFrom":[subQ1,subQ0]});Q19=makeQuery(id+"F7.imprint","IMPRINT",FACE,{"disambiguationData":[TD([[makeQuery(id+"F7.imprint","IMPRINT",EDGE,{"disambiguationData":[TD([[subQ2,-1.0]])],"derivedFrom":subQ1}),-1.0]])]});}
            extrude(context, id + "F8", {"entities" : qUnion([Q0, Q1, Q2, Q3, Q4, Q5, Q6, Q7, Q8, Q9, Q10, Q11, Q12, Q13, Q14, Q15, Q16, Q17, Q18, Q19]), "depth" : 12 * mm});
        }
        {
            var Q0;
            {var subQ1=sQuery(id+"F5.wireOp",EDGE,"E108");Q0=makeQuery(id+"F5.imprint","IMPRINT",FACE,{"disambiguationData":[TD([[makeQuery(id+"F5.imprint","IMPRINT",EDGE,{"derivedFrom":subQ1}),1.0]])]});}
            var sketch = newSketch(context, id + "F9", { "sketchPlane" : qUnion([Q0])});
            skLineSegment(sketch, "E202", {"start": v(-284.42, 419.18) * mm, "end": v(-267.1, 429.18) * mm});
            skLineSegment(sketch, "E203", {"start": v(-267.1, 429.18) * mm, "end": v(-225.66, 500.96) * mm});
            skLineSegment(sketch, "E204", {"start": v(-225.66, 500.96) * mm, "end": v(-225.66, 520.96) * mm});
            skArc(sketch, "E205", {"start": v(-271.01, 525.28) * mm, "mid": v(-248.44, 522.04) * mm, "end": v(-225.66, 520.96) * mm});
            skArc(sketch, "E206", {"start": v(-271.01, 525.28) * mm, "mid": v(-315.5, 504.98) * mm, "end": v(-310.84, 456.3) * mm});
            skArc(sketch, "E207", {"start": v(-284.42, 419.18) * mm, "mid": v(-296.75, 438.36) * mm, "end": v(-310.84, 456.3) * mm});
            skSolve(sketch);
        }
        {
            var Q0;
            {var subQ5=sQuery(id+"F9.wireOp",EDGE,"E203");Q0=makeQuery(id+"F9.imprint","IMPRINT",FACE,{"disambiguationData":[TD([[makeQuery(id+"F9.imprint","IMPRINT",EDGE,{"derivedFrom":subQ5}),1.0]])]});}
            extrude(context, id + "F10", {"entities" : qUnion([Q0]), "depth" : 2 * mm});
        }
        {
            var Q0;
            Q0=makeQuery(id+"F10.opExtrude","CAP_FACE",FACE,{"disambiguationData":[OSD([sQuery(id+"F5.wireOp",EDGE,"E138"),sQuery(id+"F5.wireOp",EDGE,"E139"),sQuery(id+"F5.wireOp",EDGE,"E140"),sQuery(id+"F5.wireOp",EDGE,"E141"),sQuery(id+"F9.wireOp",EDGE,"E202"),sQuery(id+"F9.wireOp",EDGE,"E203"),sQuery(id+"F9.wireOp",EDGE,"E204"),sQuery(id+"F9.wireOp",EDGE,"E205"),sQuery(id+"F9.wireOp",EDGE,"E206"),sQuery(id+"F9.wireOp",EDGE,"E207")])],"isStart":false});
            var sketch = newSketch(context, id + "F11", { "sketchPlane" : qUnion([Q0])});
            skPoint(sketch, "E208", {"position": v(-282.63, 425.98) * mm});
            skPoint(sketch, "E209", {"position": v(-270.76, 432.84) * mm});
            skPoint(sketch, "E210", {"position": v(-230.66, 502.3) * mm});
            skPoint(sketch, "E211", {"position": v(-230.66, 516) * mm});
            skLineSegment(sketch, "E212", {"start": v(-270.76, 432.84) * mm, "end": v(-282.63, 425.98) * mm});
            skLineSegment(sketch, "E213", {"start": v(-270.76, 432.84) * mm, "end": v(-230.66, 502.3) * mm});
            skLineSegment(sketch, "E214", {"start": v(-230.66, 502.3) * mm, "end": v(-230.66, 516) * mm});
            skArc(sketch, "E215", {"start": v(-282.63, 425.98) * mm, "mid": v(-294.13, 443.3) * mm, "end": v(-307.06, 459.57) * mm});
            skPoint(sketch, "E216", {"position": v(-307.06, 459.57) * mm});
            skLineSegment(sketch, "E217", {"start": v(-310.84, 456.3) * mm, "end": v(-307.06, 459.57) * mm});
            skPoint(sketch, "E218", {"position": v(-294.13, 443.3) * mm});
            skLineSegment(sketch, "E219", {"start": v(-294.13, 443.3) * mm, "end": v(-298.18, 440.35) * mm});
            skLineSegment(sketch, "E220", {"start": v(-271.01, 525.28) * mm, "end": v(-271.96, 520.37) * mm});
            skArc(sketch, "E221", {"start": v(-271.96, 520.37) * mm, "mid": v(-251.4, 517.31) * mm, "end": v(-230.66, 516) * mm});
            skLineSegment(sketch, "E222", {"start": v(-251.4, 517.31) * mm, "end": v(-250.87, 522.29) * mm});
            skArc(sketch, "E223", {"start": v(-271.96, 520.37) * mm, "mid": v(-311.17, 502.48) * mm, "end": v(-307.06, 459.57) * mm});
            skLineSegment(sketch, "E224", {"start": v(-311.17, 502.48) * mm, "end": v(-315.5, 504.98) * mm});
            skLineSegment(sketch, "E225", {"start": v(-270.76, 432.84) * mm, "end": v(-267.1, 429.18) * mm});
            skLineSegment(sketch, "E226", {"start": v(-230.66, 502.3) * mm, "end": v(-225.66, 500.96) * mm});
            skSolve(sketch);
        }
        {
            var Q0;
            {var subQ0=sQuery(id+"F11.wireOp",EDGE,"E217");Q0=makeQuery(id+"F11.imprint","IMPRINT",FACE,{"disambiguationData":[TD([[makeQuery(id+"F11.imprint","IMPRINT",EDGE,{"derivedFrom":subQ0}),-1.0]])]});}
            var Q1;
            {var subQ4=sQuery(id+"F11.wireOp",EDGE,"E212");Q1=makeQuery(id+"F11.imprint","IMPRINT",FACE,{"disambiguationData":[TD([[makeQuery(id+"F11.imprint","IMPRINT",EDGE,{"derivedFrom":subQ4}),1.0]])]});}
            var Q2;
            {var subQ1=sQuery(id+"F11.wireOp",EDGE,"E217");Q2=makeQuery(id+"F11.imprint","IMPRINT",FACE,{"disambiguationData":[TD([[makeQuery(id+"F11.imprint","IMPRINT",EDGE,{"derivedFrom":subQ1}),1.0]])]});}
            var Q3;
            {var subQ5=sQuery(id+"F11.wireOp",EDGE,"E220");Q3=makeQuery(id+"F11.imprint","IMPRINT",FACE,{"disambiguationData":[TD([[makeQuery(id+"F11.imprint","IMPRINT",EDGE,{"derivedFrom":subQ5}),-1.0]])]});}
            var Q4;
            {var subQ0=sQuery(id+"F11.wireOp",EDGE,"E220");Q4=makeQuery(id+"F11.imprint","IMPRINT",FACE,{"disambiguationData":[TD([[makeQuery(id+"F11.imprint","IMPRINT",EDGE,{"derivedFrom":subQ0}),1.0]])]});}
            var Q5;
            {var subQ2=sQuery(id+"F11.wireOp",EDGE,"E214");Q5=makeQuery(id+"F11.imprint","IMPRINT",FACE,{"disambiguationData":[TD([[makeQuery(id+"F11.imprint","IMPRINT",EDGE,{"derivedFrom":subQ2}),-1.0]])]});}
            extrude(context, id + "F12", {"entities" : qUnion([Q0, Q1, Q2, Q3, Q4, Q5]), "operationType" : NewBodyOperationType.ADD, "depth" : (12 - 2) * mm});
        }
        {
            var Q0;
            Q0=makeQuery(id+"F10.opExtrude","CAP_EDGE",EDGE,{"disambiguationData":[OSD([sQuery(id+"F9.wireOp",EDGE,"E203")])],"isStart":false});
            fillet(context, id + "F13", {"entities" : qUnion([Q0]), "radius" : 2 * mm, "tangentPropagation" : true, "allowEdgeOverflow" : false});
        }
        {
            var Q0;
            Q0=makeQuery(id+"F12.opExtrude","SWEPT_EDGE",EDGE,{"disambiguationData":[OSD([sQuery(id+"F11.wireOp",EDGE,"E212"),sQuery(id+"F11.wireOp",EDGE,"E213"),sQuery(id+"F11.wireOp",EDGE,"E225")])]});
            var Q1;
            Q1=makeQuery(id+"F12.opExtrude","SWEPT_EDGE",EDGE,{"disambiguationData":[OSD([sQuery(id+"F11.wireOp",EDGE,"E213"),sQuery(id+"F11.wireOp",EDGE,"E214"),sQuery(id+"F11.wireOp",EDGE,"E226")])]});
            fillet(context, id + "F14", {"entities" : qUnion([Q0, Q1]), "radius" : 5 * mm, "tangentPropagation" : true, "allowEdgeOverflow" : false});
        }
        {
            var Q0;
            Q0=makeQuery(id+"F8.opExtrude","SWEPT_EDGE",EDGE,{"disambiguationData":[OSD([sQuery(id+"F7.wireOp",EDGE,"E199"),sQuery(id+"F7.wireOp",EDGE,"E200")])]});
            var Q1;
            Q1=makeQuery(id+"F8.opExtrude","SWEPT_EDGE",EDGE,{"disambiguationData":[OSD([sQuery(id+"F7.wireOp",EDGE,"E200"),sQuery(id+"F7.wireOp",EDGE,"E201")])]});
            var Q2;
            Q2=makeQuery(id+"F8.opExtrude","SWEPT_EDGE",EDGE,{"disambiguationData":[OSD([sQuery(id+"F7.wireOp",EDGE,"E198"),sQuery(id+"F7.wireOp",EDGE,"E201")])]});
            var Q3;
            Q3=makeQuery(id+"F8.opExtrude","SWEPT_EDGE",EDGE,{"disambiguationData":[OSD([sQuery(id+"F7.wireOp",EDGE,"E198"),sQuery(id+"F7.wireOp",EDGE,"E199")])]});
            var Q4;
            Q4=makeQuery(id+"F8.opExtrude","SWEPT_EDGE",EDGE,{"disambiguationData":[OSD([sQuery(id+"F7.wireOp",EDGE,"E186"),sQuery(id+"F7.wireOp",EDGE,"E187")])]});
            var Q5;
            Q5=makeQuery(id+"F8.opExtrude","SWEPT_EDGE",EDGE,{"disambiguationData":[OSD([sQuery(id+"F7.wireOp",EDGE,"E187"),sQuery(id+"F7.wireOp",EDGE,"E188")])]});
            var Q6;
            Q6=makeQuery(id+"F8.opExtrude","SWEPT_EDGE",EDGE,{"disambiguationData":[OSD([sQuery(id+"F7.wireOp",EDGE,"E188"),sQuery(id+"F7.wireOp",EDGE,"E189")])]});
            var Q7;
            Q7=makeQuery(id+"F8.opExtrude","SWEPT_EDGE",EDGE,{"disambiguationData":[OSD([sQuery(id+"F7.wireOp",EDGE,"E186"),sQuery(id+"F7.wireOp",EDGE,"E189")])]});
            var Q8;
            Q8=makeQuery(id+"F8.opExtrude","SWEPT_EDGE",EDGE,{"disambiguationData":[OSD([sQuery(id+"F7.wireOp",EDGE,"E196"),sQuery(id+"F7.wireOp",EDGE,"E197")])]});
            var Q9;
            Q9=makeQuery(id+"F8.opExtrude","SWEPT_EDGE",EDGE,{"disambiguationData":[OSD([sQuery(id+"F7.wireOp",EDGE,"E190"),sQuery(id+"F7.wireOp",EDGE,"E191")])]});
            var Q10;
            Q10=makeQuery(id+"F8.opExtrude","SWEPT_EDGE",EDGE,{"disambiguationData":[OSD([sQuery(id+"F7.wireOp",EDGE,"E191"),sQuery(id+"F7.wireOp",EDGE,"E192")])]});
            var Q11;
            Q11=makeQuery(id+"F8.opExtrude","SWEPT_EDGE",EDGE,{"disambiguationData":[OSD([sQuery(id+"F7.wireOp",EDGE,"E192"),sQuery(id+"F7.wireOp",EDGE,"E193")])]});
            var Q12;
            Q12=makeQuery(id+"F8.opExtrude","SWEPT_EDGE",EDGE,{"disambiguationData":[OSD([sQuery(id+"F7.wireOp",EDGE,"E190"),sQuery(id+"F7.wireOp",EDGE,"E193")])]});
            var Q13;
            Q13=makeQuery(id+"F8.opExtrude","SWEPT_EDGE",EDGE,{"disambiguationData":[OSD([sQuery(id+"F7.wireOp",EDGE,"E194"),sQuery(id+"F7.wireOp",EDGE,"E195")])]});
            var Q14;
            Q14=makeQuery(id+"F8.opExtrude","SWEPT_EDGE",EDGE,{"disambiguationData":[OSD([sQuery(id+"F7.wireOp",EDGE,"E195"),sQuery(id+"F7.wireOp",EDGE,"E196")])]});
            var Q15;
            Q15=makeQuery(id+"F8.opExtrude","SWEPT_EDGE",EDGE,{"disambiguationData":[OSD([sQuery(id+"F7.wireOp",EDGE,"E194"),sQuery(id+"F7.wireOp",EDGE,"E197")])]});
            var Q16;
            Q16=makeQuery(id+"F8.opExtrude","SWEPT_FACE",FACE,{"disambiguationData":[OSD([sQuery(id+"F7.wireOp",EDGE,"E200")])]});
            var Q17;
            Q17=makeQuery(id+"F8.opExtrude","SWEPT_FACE",FACE,{"disambiguationData":[OSD([sQuery(id+"F7.wireOp",EDGE,"E187")])]});
            var Q18;
            Q18=makeQuery(id+"F8.opExtrude","SWEPT_FACE",FACE,{"disambiguationData":[OSD([sQuery(id+"F7.wireOp",EDGE,"E196")])]});
            var Q19;
            Q19=makeQuery(id+"F8.opExtrude","SWEPT_FACE",FACE,{"disambiguationData":[OSD([sQuery(id+"F7.wireOp",EDGE,"E191")])]});
            var Q20;
            Q20=makeQuery(id+"F12.opExtrude","CAP_EDGE",EDGE,{"disambiguationData":[OSD([sQuery(id+"F11.wireOp",EDGE,"E212")])],"isStart":false});
            var Q21;
            Q21=makeQuery(id+"F12.opExtrude","CAP_EDGE",EDGE,{"disambiguationData":[OSD([sQuery(id+"F11.wireOp",EDGE,"E215")])],"isStart":false});
            var Q22;
            Q22=makeQuery(id+"F12.opExtrude","CAP_EDGE",EDGE,{"disambiguationData":[OSD([sQuery(id+"F11.wireOp",EDGE,"E221")])],"isStart":false});
            var Q23;
            Q23=makeQuery(id+"F12.opExtrude","CAP_EDGE",EDGE,{"disambiguationData":[OSD([sQuery(id+"F11.wireOp",EDGE,"E214")])],"isStart":false});
            fillet(context, id + "F15", {"entities" : qUnion([Q0, Q1, Q2, Q3, Q4, Q5, Q6, Q7, Q8, Q9, Q10, Q11, Q12, Q13, Q14, Q15, Q16, Q17, Q18, Q19, Q20, Q21, Q22, Q23]), "radius" : 1 * mm, "tangentPropagation" : true, "allowEdgeOverflow" : false});
        }
    });
